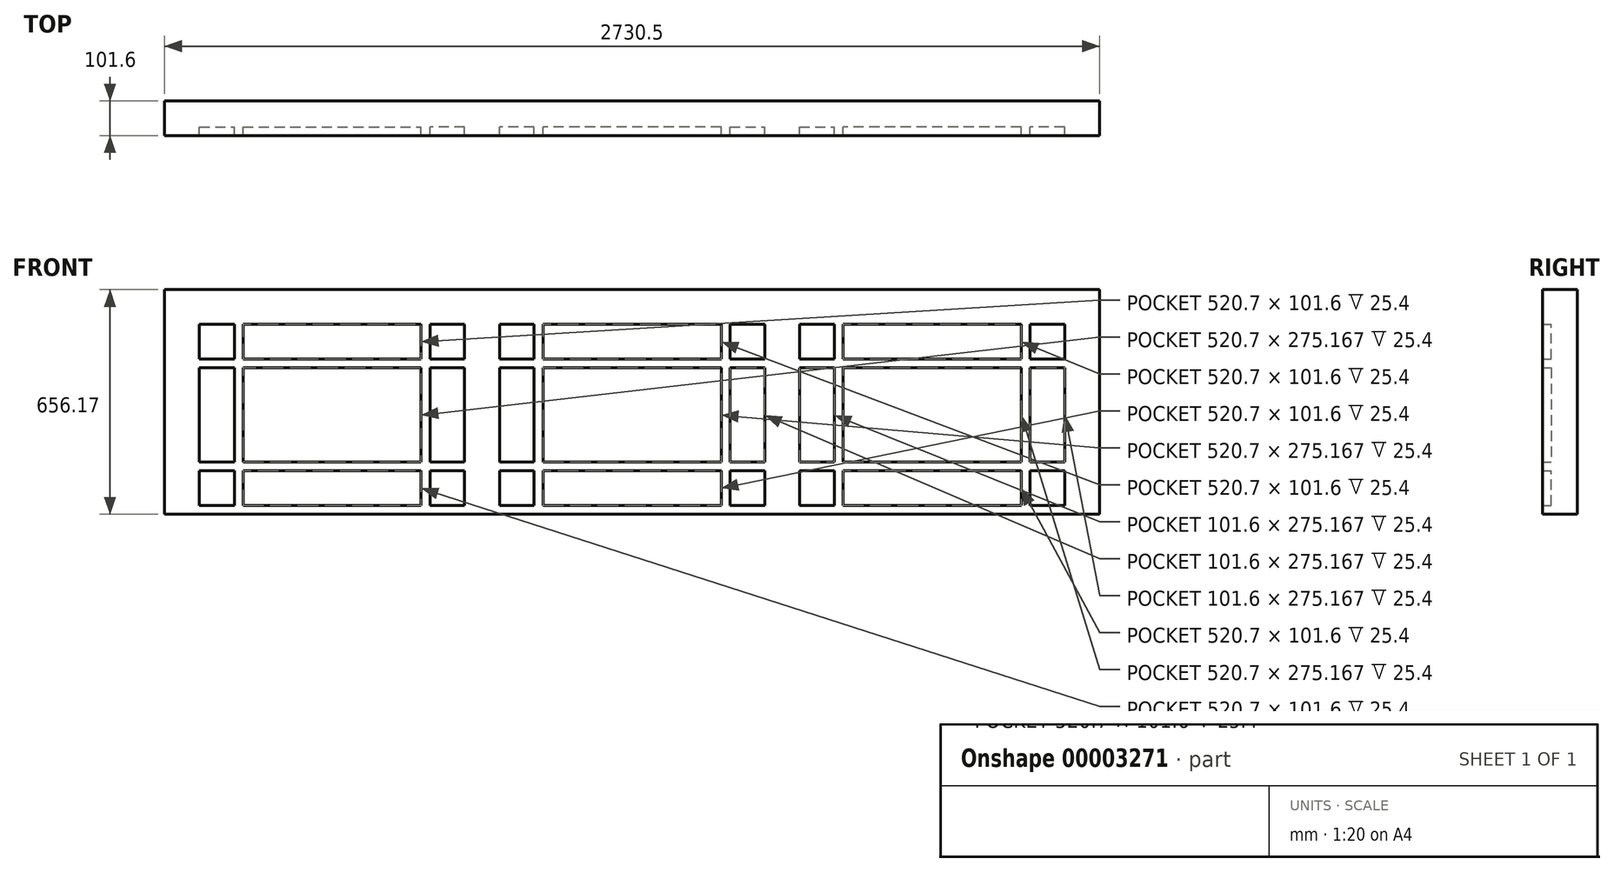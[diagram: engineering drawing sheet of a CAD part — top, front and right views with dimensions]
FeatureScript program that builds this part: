
annotation { "Feature Type Name" : "Feature", "Feature Type Description" : "" }
export const myFeature = defineFeature(function(context is Context, id is Id, definition is map)
    precondition{}
    {
        {
            var Q0;
            Q0=qCreatedBy(makeId("Front.planeOp"),FACE);
            var sketch = newSketch(context, id + "F0", { "sketchPlane" : qUnion([Q0])});
            skLineSegment(sketch, "E0.bottom", {"start": v(0, 0) * mm, "end": v(2730.5, 0) * mm});
            skLineSegment(sketch, "E0.top", {"start": v(0, 656.17) * mm, "end": v(2730.5, 656.17) * mm});
            skLineSegment(sketch, "E0.left", {"start": v(0, 0) * mm, "end": v(0, 656.17) * mm});
            skLineSegment(sketch, "E0.right", {"start": v(2730.5, 0) * mm, "end": v(2730.5, 656.17) * mm});
            skSolve(sketch);
        }
        {
            var Q0;
            Q0=makeQuery(id+"F0.imprint","IMPRINT",FACE,{"disambiguationData":[TD([[makeQuery(id+"F0.imprint","IMPRINT",EDGE,{"derivedFrom":sQuery(id+"F0.wireOp",EDGE,"E0.bottom")}),1.0]])]});
            extrude(context, id + "F1", {"entities" : qUnion([Q0]), "depth" : 76.2 * mm});
        }
        {
            var Q0;
            Q0=makeQuery(id+"F1.opExtrude","CAP_FACE",FACE,{"disambiguationData":[OSD([sQuery(id+"F0.wireOp",EDGE,"E0.bottom"),sQuery(id+"F0.wireOp",EDGE,"E0.top"),sQuery(id+"F0.wireOp",EDGE,"E0.left"),sQuery(id+"F0.wireOp",EDGE,"E0.right")])],"isStart":false});
            var sketch = newSketch(context, id + "F2", { "sketchPlane" : qUnion([Q0])});
            skLineSegment(sketch, "E1.0", {"start": v(2628.9, 25.4) * mm, "end": v(2628.9, 554.57) * mm, "construction": true});
            skLineSegment(sketch, "E1.1", {"start": v(101.6, 554.57) * mm, "end": v(876.3, 554.57) * mm, "construction": true});
            skLineSegment(sketch, "E1.2", {"start": v(101.6, 25.4) * mm, "end": v(101.6, 554.57) * mm, "construction": true});
            skLineSegment(sketch, "E2.0", {"start": v(101.6, 25.4) * mm, "end": v(876.3, 25.4) * mm, "construction": true});
            skLineSegment(sketch, "E3", {"start": v(876.3, 554.57) * mm, "end": v(876.3, 25.4) * mm, "construction": true});
            skLineSegment(sketch, "E4", {"start": v(977.9, 554.57) * mm, "end": v(977.9, 25.4) * mm, "construction": true});
            skLineSegment(sketch, "E5", {"start": v(1752.6, 554.57) * mm, "end": v(1752.6, 25.4) * mm, "construction": true});
            skLineSegment(sketch, "E6", {"start": v(1854.2, 554.57) * mm, "end": v(1854.2, 25.4) * mm, "construction": true});
            skLineSegment(sketch, "E7", {"start": v(876.3, 554.57) * mm, "end": v(977.9, 554.57) * mm, "construction": true});
            skLineSegment(sketch, "E8", {"start": v(977.9, 554.57) * mm, "end": v(1752.6, 554.57) * mm, "construction": true});
            skLineSegment(sketch, "E9", {"start": v(1752.6, 554.57) * mm, "end": v(1854.2, 554.57) * mm, "construction": true});
            skLineSegment(sketch, "E10", {"start": v(1854.2, 554.57) * mm, "end": v(2628.9, 554.57) * mm, "construction": true});
            skLineSegment(sketch, "E11", {"start": v(1854.2, 25.4) * mm, "end": v(2628.9, 25.4) * mm, "construction": true});
            skLineSegment(sketch, "E12", {"start": v(977.9, 25.4) * mm, "end": v(1752.6, 25.4) * mm, "construction": true});
            skLineSegment(sketch, "E13", {"start": v(101.6, 554.57) * mm, "end": v(0, 554.57) * mm, "construction": true});
            skPoint(sketch, "E14", {"position": v(488.95, 554.57) * mm});
            skLineSegment(sketch, "E15", {"start": v(488.95, 554.57) * mm, "end": v(488.95, 25.4) * mm, "construction": true});
            skPoint(sketch, "E16", {"position": v(927.1, 554.57) * mm});
            skLineSegment(sketch, "E17", {"start": v(927.1, 554.57) * mm, "end": v(927.1, 0) * mm, "construction": true});
            skPoint(sketch, "E18", {"position": v(101.6, 289.98) * mm});
            skLineSegment(sketch, "E19", {"start": v(101.6, 289.98) * mm, "end": v(876.3, 289.98) * mm, "construction": true});
            skLineSegment(sketch, "E20", {"start": v(101.6, 554.57) * mm, "end": v(203.2, 554.57) * mm});
            skLineSegment(sketch, "E21", {"start": v(203.2, 554.57) * mm, "end": v(203.2, 452.97) * mm});
            skLineSegment(sketch, "E22", {"start": v(203.2, 452.97) * mm, "end": v(101.6, 452.97) * mm});
            skLineSegment(sketch, "E23", {"start": v(101.6, 452.97) * mm, "end": v(101.6, 554.57) * mm});
            skLineSegment(sketch, "E24", {"start": v(488.95, 554.57) * mm, "end": v(228.6, 554.57) * mm});
            skLineSegment(sketch, "E25", {"start": v(228.6, 554.57) * mm, "end": v(228.6, 452.97) * mm});
            skLineSegment(sketch, "E26", {"start": v(228.6, 452.97) * mm, "end": v(488.95, 452.97) * mm});
            skLineSegment(sketch, "E27", {"start": v(203.2, 289.98) * mm, "end": v(203.2, 427.57) * mm});
            skLineSegment(sketch, "E28", {"start": v(203.2, 427.57) * mm, "end": v(101.6, 427.57) * mm});
            skLineSegment(sketch, "E29", {"start": v(101.6, 427.57) * mm, "end": v(101.6, 289.98) * mm});
            skLineSegment(sketch, "E30", {"start": v(203.2, 554.57) * mm, "end": v(228.6, 554.57) * mm, "construction": true});
            skLineSegment(sketch, "E31", {"start": v(101.6, 427.57) * mm, "end": v(101.6, 452.97) * mm, "construction": true});
            skLineSegment(sketch, "E32", {"start": v(203.2, 289.98) * mm, "end": v(228.6, 289.98) * mm, "construction": true});
            skLineSegment(sketch, "E33", {"start": v(228.6, 289.98) * mm, "end": v(228.6, 427.57) * mm});
            skLineSegment(sketch, "E34", {"start": v(228.6, 427.57) * mm, "end": v(488.95, 427.57) * mm});
            skLineSegment(sketch, "E35.0.MirrorCS", {"start": v(488.95, 25.4) * mm, "end": v(228.6, 25.4) * mm});
            skLineSegment(sketch, "E35.1.MirrorCS", {"start": v(228.6, 25.4) * mm, "end": v(228.6, 127) * mm});
            skLineSegment(sketch, "E35.2.MirrorCS", {"start": v(228.6, 127) * mm, "end": v(488.95, 127) * mm});
            skLineSegment(sketch, "E35.3.MirrorCS", {"start": v(228.6, 152.4) * mm, "end": v(488.95, 152.4) * mm});
            skLineSegment(sketch, "E35.4.MirrorCS", {"start": v(228.6, 289.98) * mm, "end": v(228.6, 152.4) * mm});
            skLineSegment(sketch, "E35.5.MirrorCS", {"start": v(203.2, 289.98) * mm, "end": v(203.2, 152.4) * mm});
            skLineSegment(sketch, "E35.6.MirrorCS", {"start": v(203.2, 152.4) * mm, "end": v(101.6, 152.4) * mm});
            skLineSegment(sketch, "E35.7.MirrorCS", {"start": v(101.6, 152.4) * mm, "end": v(101.6, 289.98) * mm});
            skLineSegment(sketch, "E35.8.MirrorCS", {"start": v(203.2, 127) * mm, "end": v(101.6, 127) * mm});
            skLineSegment(sketch, "E35.9.MirrorCS", {"start": v(203.2, 25.4) * mm, "end": v(203.2, 127) * mm});
            skLineSegment(sketch, "E35.10.MirrorCS", {"start": v(101.6, 127) * mm, "end": v(101.6, 25.4) * mm});
            skLineSegment(sketch, "E35.11.MirrorCS", {"start": v(101.6, 25.4) * mm, "end": v(203.2, 25.4) * mm});
            skLineSegment(sketch, "E36.0.MirrorCS", {"start": v(488.95, 554.57) * mm, "end": v(749.3, 554.57) * mm});
            skLineSegment(sketch, "E37.0.MirrorCS", {"start": v(749.3, 554.57) * mm, "end": v(749.3, 452.97) * mm});
            skLineSegment(sketch, "E38.0.MirrorCS", {"start": v(749.3, 452.97) * mm, "end": v(488.95, 452.97) * mm});
            skLineSegment(sketch, "E39.0.MirrorCS", {"start": v(749.3, 427.57) * mm, "end": v(488.95, 427.57) * mm});
            skLineSegment(sketch, "E40.0.MirrorCS", {"start": v(749.3, 289.98) * mm, "end": v(749.3, 427.57) * mm});
            skLineSegment(sketch, "E41.0.MirrorCS", {"start": v(749.3, 289.98) * mm, "end": v(749.3, 152.4) * mm});
            skLineSegment(sketch, "E42.0.MirrorCS", {"start": v(749.3, 152.4) * mm, "end": v(488.95, 152.4) * mm});
            skLineSegment(sketch, "E43.0.MirrorCS", {"start": v(749.3, 127) * mm, "end": v(488.95, 127) * mm});
            skLineSegment(sketch, "E44.0.MirrorCS", {"start": v(749.3, 25.4) * mm, "end": v(749.3, 127) * mm});
            skLineSegment(sketch, "E45.0.MirrorCS", {"start": v(488.95, 25.4) * mm, "end": v(749.3, 25.4) * mm});
            skLineSegment(sketch, "E46.0.MirrorCS", {"start": v(876.3, 25.4) * mm, "end": v(774.7, 25.4) * mm});
            skLineSegment(sketch, "E47.0.MirrorCS", {"start": v(876.3, 127) * mm, "end": v(876.3, 25.4) * mm});
            skLineSegment(sketch, "E48.0.MirrorCS", {"start": v(774.7, 127) * mm, "end": v(876.3, 127) * mm});
            skLineSegment(sketch, "E49.0.MirrorCS", {"start": v(774.7, 25.4) * mm, "end": v(774.7, 127) * mm});
            skLineSegment(sketch, "E50.0.MirrorCS", {"start": v(774.7, 152.4) * mm, "end": v(876.3, 152.4) * mm});
            skLineSegment(sketch, "E51.0.MirrorCS", {"start": v(876.3, 152.4) * mm, "end": v(876.3, 289.98) * mm});
            skLineSegment(sketch, "E52.0.MirrorCS", {"start": v(876.3, 427.57) * mm, "end": v(876.3, 289.98) * mm});
            skLineSegment(sketch, "E53.0.MirrorCS", {"start": v(774.7, 427.57) * mm, "end": v(876.3, 427.57) * mm});
            skLineSegment(sketch, "E54.0.MirrorCS", {"start": v(774.7, 452.97) * mm, "end": v(876.3, 452.97) * mm});
            skLineSegment(sketch, "E55.0.MirrorCS", {"start": v(876.3, 452.97) * mm, "end": v(876.3, 554.57) * mm});
            skLineSegment(sketch, "E56.0.MirrorCS", {"start": v(876.3, 554.57) * mm, "end": v(774.7, 554.57) * mm});
            skLineSegment(sketch, "E57.0.MirrorCS", {"start": v(774.7, 554.57) * mm, "end": v(774.7, 452.97) * mm});
            skLineSegment(sketch, "E58.0.MirrorCS", {"start": v(774.7, 289.98) * mm, "end": v(774.7, 427.57) * mm});
            skLineSegment(sketch, "E59.0.MirrorCS", {"start": v(774.7, 289.98) * mm, "end": v(774.7, 152.4) * mm});
            skPoint(sketch, "E60", {"position": v(1365.25, 656.17) * mm});
            skLineSegment(sketch, "E61", {"start": v(1365.25, 656.17) * mm, "end": v(1365.25, 0) * mm, "construction": true});
            skLineSegment(sketch, "E62.0.MirrorCS", {"start": v(1854.2, 25.4) * mm, "end": v(1955.8, 25.4) * mm});
            skLineSegment(sketch, "E63.0.MirrorCS", {"start": v(2241.55, 25.4) * mm, "end": v(1981.2, 25.4) * mm});
            skLineSegment(sketch, "E64.0.MirrorCS", {"start": v(2241.55, 25.4) * mm, "end": v(2501.9, 25.4) * mm});
            skLineSegment(sketch, "E65.0.MirrorCS", {"start": v(2628.9, 25.4) * mm, "end": v(2527.3, 25.4) * mm});
            skLineSegment(sketch, "E66.0.MirrorCS", {"start": v(1854.2, 554.57) * mm, "end": v(1955.8, 554.57) * mm});
            skLineSegment(sketch, "E67.0.MirrorCS", {"start": v(2241.55, 554.57) * mm, "end": v(1981.2, 554.57) * mm});
            skLineSegment(sketch, "E68.0.MirrorCS", {"start": v(2241.55, 554.57) * mm, "end": v(2501.9, 554.57) * mm});
            skLineSegment(sketch, "E69.0.MirrorCS", {"start": v(2501.9, 452.97) * mm, "end": v(2241.55, 452.97) * mm});
            skLineSegment(sketch, "E70.0.MirrorCS", {"start": v(1981.2, 127) * mm, "end": v(2241.55, 127) * mm});
            skLineSegment(sketch, "E71.0.MirrorCS", {"start": v(1955.8, 289.98) * mm, "end": v(1955.8, 152.4) * mm});
            skLineSegment(sketch, "E72.0.MirrorCS", {"start": v(1854.2, 152.4) * mm, "end": v(1854.2, 289.98) * mm});
            skLineSegment(sketch, "E73.0.MirrorCS", {"start": v(1955.8, 152.4) * mm, "end": v(1854.2, 152.4) * mm});
            skLineSegment(sketch, "E74.0.MirrorCS", {"start": v(1955.8, 289.98) * mm, "end": v(1955.8, 427.57) * mm});
            skLineSegment(sketch, "E75.0.MirrorCS", {"start": v(1854.2, 427.57) * mm, "end": v(1854.2, 289.98) * mm});
            skLineSegment(sketch, "E76.0.MirrorCS", {"start": v(1854.2, 452.97) * mm, "end": v(1854.2, 554.57) * mm});
            skLineSegment(sketch, "E77.0.MirrorCS", {"start": v(1955.8, 554.57) * mm, "end": v(1955.8, 452.97) * mm});
            skLineSegment(sketch, "E78.0.MirrorCS", {"start": v(1981.2, 554.57) * mm, "end": v(1981.2, 452.97) * mm});
            skLineSegment(sketch, "E79.0.MirrorCS", {"start": v(1981.2, 452.97) * mm, "end": v(2241.55, 452.97) * mm});
            skLineSegment(sketch, "E80.0.MirrorCS", {"start": v(2501.9, 554.57) * mm, "end": v(2501.9, 452.97) * mm});
            skLineSegment(sketch, "E81.0.MirrorCS", {"start": v(2527.3, 554.57) * mm, "end": v(2527.3, 452.97) * mm});
            skLineSegment(sketch, "E82.0.MirrorCS", {"start": v(2628.9, 554.57) * mm, "end": v(2527.3, 554.57) * mm});
            skLineSegment(sketch, "E83.0.MirrorCS", {"start": v(2628.9, 452.97) * mm, "end": v(2628.9, 554.57) * mm});
            skLineSegment(sketch, "E84.0.MirrorCS", {"start": v(2527.3, 452.97) * mm, "end": v(2628.9, 452.97) * mm});
            skLineSegment(sketch, "E85.0.MirrorCS", {"start": v(2527.3, 427.57) * mm, "end": v(2628.9, 427.57) * mm});
            skLineSegment(sketch, "E86.0.MirrorCS", {"start": v(2628.9, 427.57) * mm, "end": v(2628.9, 289.98) * mm});
            skLineSegment(sketch, "E87.0.MirrorCS", {"start": v(1955.8, 127) * mm, "end": v(1854.2, 127) * mm});
            skLineSegment(sketch, "E88.0.MirrorCS", {"start": v(1955.8, 25.4) * mm, "end": v(1955.8, 127) * mm});
            skLineSegment(sketch, "E89.0.MirrorCS", {"start": v(1981.2, 25.4) * mm, "end": v(1981.2, 127) * mm});
            skLineSegment(sketch, "E90.0.MirrorCS", {"start": v(2628.9, 152.4) * mm, "end": v(2628.9, 289.98) * mm});
            skLineSegment(sketch, "E91.0.MirrorCS", {"start": v(2527.3, 152.4) * mm, "end": v(2628.9, 152.4) * mm});
            skLineSegment(sketch, "E92.0.MirrorCS", {"start": v(2501.9, 152.4) * mm, "end": v(2241.55, 152.4) * mm});
            skLineSegment(sketch, "E93.0.MirrorCS", {"start": v(1981.2, 152.4) * mm, "end": v(2241.55, 152.4) * mm});
            skLineSegment(sketch, "E94.0.MirrorCS", {"start": v(1981.2, 289.98) * mm, "end": v(1981.2, 152.4) * mm});
            skLineSegment(sketch, "E95.0.MirrorCS", {"start": v(1981.2, 289.98) * mm, "end": v(1981.2, 427.57) * mm});
            skLineSegment(sketch, "E96.0.MirrorCS", {"start": v(1981.2, 427.57) * mm, "end": v(2241.55, 427.57) * mm});
            skLineSegment(sketch, "E97.0.MirrorCS", {"start": v(2501.9, 427.57) * mm, "end": v(2241.55, 427.57) * mm});
            skLineSegment(sketch, "E98.0.MirrorCS", {"start": v(2501.9, 289.98) * mm, "end": v(2501.9, 427.57) * mm});
            skLineSegment(sketch, "E99.0.MirrorCS", {"start": v(2501.9, 289.98) * mm, "end": v(2501.9, 152.4) * mm});
            skLineSegment(sketch, "E100.0.MirrorCS", {"start": v(2501.9, 127) * mm, "end": v(2241.55, 127) * mm});
            skLineSegment(sketch, "E101.0.MirrorCS", {"start": v(2501.9, 25.4) * mm, "end": v(2501.9, 127) * mm});
            skLineSegment(sketch, "E102.0.MirrorCS", {"start": v(2527.3, 25.4) * mm, "end": v(2527.3, 127) * mm});
            skLineSegment(sketch, "E103.0.MirrorCS", {"start": v(2628.9, 127) * mm, "end": v(2628.9, 25.4) * mm});
            skLineSegment(sketch, "E104.0.MirrorCS", {"start": v(2527.3, 127) * mm, "end": v(2628.9, 127) * mm});
            skLineSegment(sketch, "E105.0.MirrorCS", {"start": v(2527.3, 289.98) * mm, "end": v(2527.3, 152.4) * mm});
            skLineSegment(sketch, "E106.0.MirrorCS", {"start": v(2527.3, 289.98) * mm, "end": v(2527.3, 427.57) * mm});
            skLineSegment(sketch, "E107", {"start": v(1854.2, 127) * mm, "end": v(1854.2, 25.4) * mm});
            skPoint(sketch, "E108", {"position": v(1803.4, 554.57) * mm});
            skLineSegment(sketch, "E109", {"start": v(1803.4, 554.57) * mm, "end": v(1803.4, 0) * mm, "construction": true});
            skLineSegment(sketch, "E110.0.MirrorCS", {"start": v(1625.6, 427.57) * mm, "end": v(1365.25, 427.57) * mm});
            skLineSegment(sketch, "E111.0.MirrorCS", {"start": v(1625.6, 289.98) * mm, "end": v(1625.6, 427.57) * mm});
            skLineSegment(sketch, "E112.0.MirrorCS", {"start": v(1625.6, 289.98) * mm, "end": v(1625.6, 152.4) * mm});
            skLineSegment(sketch, "E113.0.MirrorCS", {"start": v(1625.6, 152.4) * mm, "end": v(1365.25, 152.4) * mm});
            skLineSegment(sketch, "E114.0.MirrorCS", {"start": v(1104.9, 152.4) * mm, "end": v(1365.25, 152.4) * mm});
            skLineSegment(sketch, "E115.0.MirrorCS", {"start": v(977.9, 127) * mm, "end": v(977.9, 25.4) * mm});
            skLineSegment(sketch, "E116.0.MirrorCS", {"start": v(977.9, 152.4) * mm, "end": v(977.9, 289.98) * mm});
            skLineSegment(sketch, "E117.0.MirrorCS", {"start": v(977.9, 427.57) * mm, "end": v(977.9, 289.98) * mm});
            skLineSegment(sketch, "E118.0.MirrorCS", {"start": v(977.9, 452.97) * mm, "end": v(977.9, 554.57) * mm});
            skLineSegment(sketch, "E119.0.MirrorCS", {"start": v(977.9, 554.57) * mm, "end": v(1079.5, 554.57) * mm});
            skLineSegment(sketch, "E120.0.MirrorCS", {"start": v(1079.5, 554.57) * mm, "end": v(1079.5, 452.97) * mm});
            skLineSegment(sketch, "E121.0.MirrorCS", {"start": v(1625.6, 127) * mm, "end": v(1365.25, 127) * mm});
            skLineSegment(sketch, "E122.0.MirrorCS", {"start": v(1104.9, 127) * mm, "end": v(1365.25, 127) * mm});
            skLineSegment(sketch, "E123.0.MirrorCS", {"start": v(1104.9, 25.4) * mm, "end": v(1104.9, 127) * mm});
            skLineSegment(sketch, "E124.0.MirrorCS", {"start": v(1365.25, 25.4) * mm, "end": v(1104.9, 25.4) * mm});
            skLineSegment(sketch, "E125.0.MirrorCS", {"start": v(1365.25, 25.4) * mm, "end": v(1625.6, 25.4) * mm});
            skLineSegment(sketch, "E126.0.MirrorCS", {"start": v(1079.5, 289.98) * mm, "end": v(1079.5, 152.4) * mm});
            skLineSegment(sketch, "E127.0.MirrorCS", {"start": v(1079.5, 289.98) * mm, "end": v(1079.5, 427.57) * mm});
            skLineSegment(sketch, "E128.0.MirrorCS", {"start": v(1079.5, 427.57) * mm, "end": v(977.9, 427.57) * mm});
            skLineSegment(sketch, "E129.0.MirrorCS", {"start": v(1079.5, 152.4) * mm, "end": v(977.9, 152.4) * mm});
            skLineSegment(sketch, "E130.0.MirrorCS", {"start": v(1104.9, 554.57) * mm, "end": v(1104.9, 452.97) * mm});
            skLineSegment(sketch, "E131.0.MirrorCS", {"start": v(1365.25, 554.57) * mm, "end": v(1104.9, 554.57) * mm});
            skLineSegment(sketch, "E132.0.MirrorCS", {"start": v(1752.6, 554.57) * mm, "end": v(1651, 554.57) * mm});
            skLineSegment(sketch, "E133.0.MirrorCS", {"start": v(1752.6, 152.4) * mm, "end": v(1752.6, 289.98) * mm});
            skLineSegment(sketch, "E134.0.MirrorCS", {"start": v(1752.6, 427.57) * mm, "end": v(1752.6, 289.98) * mm});
            skLineSegment(sketch, "E135.0.MirrorCS", {"start": v(1651, 554.57) * mm, "end": v(1651, 452.97) * mm});
            skLineSegment(sketch, "E136.0.MirrorCS", {"start": v(1079.5, 127) * mm, "end": v(977.9, 127) * mm});
            skLineSegment(sketch, "E137.0.MirrorCS", {"start": v(1079.5, 25.4) * mm, "end": v(1079.5, 127) * mm});
            skLineSegment(sketch, "E138.0.MirrorCS", {"start": v(977.9, 25.4) * mm, "end": v(1079.5, 25.4) * mm});
            skLineSegment(sketch, "E139.0.MirrorCS", {"start": v(1104.9, 427.57) * mm, "end": v(1365.25, 427.57) * mm});
            skLineSegment(sketch, "E140.0.MirrorCS", {"start": v(1625.6, 554.57) * mm, "end": v(1625.6, 452.97) * mm});
            skLineSegment(sketch, "E141.0.MirrorCS", {"start": v(1365.25, 554.57) * mm, "end": v(1625.6, 554.57) * mm});
            skLineSegment(sketch, "E142.0.MirrorCS", {"start": v(1651, 289.98) * mm, "end": v(1651, 427.57) * mm});
            skLineSegment(sketch, "E143.0.MirrorCS", {"start": v(1651, 289.98) * mm, "end": v(1651, 152.4) * mm});
            skLineSegment(sketch, "E144.0.MirrorCS", {"start": v(1651, 427.57) * mm, "end": v(1752.6, 427.57) * mm});
            skLineSegment(sketch, "E145.0.MirrorCS", {"start": v(1625.6, 25.4) * mm, "end": v(1625.6, 127) * mm});
            skLineSegment(sketch, "E146.0.MirrorCS", {"start": v(1651, 25.4) * mm, "end": v(1651, 127) * mm});
            skLineSegment(sketch, "E147.0.MirrorCS", {"start": v(1752.6, 127) * mm, "end": v(1752.6, 25.4) * mm});
            skLineSegment(sketch, "E148.0.MirrorCS", {"start": v(1651, 127) * mm, "end": v(1752.6, 127) * mm});
            skLineSegment(sketch, "E149.0.MirrorCS", {"start": v(1752.6, 25.4) * mm, "end": v(1651, 25.4) * mm});
            skLineSegment(sketch, "E150.0.MirrorCS", {"start": v(1651, 152.4) * mm, "end": v(1752.6, 152.4) * mm});
            skLineSegment(sketch, "E151.0.MirrorCS", {"start": v(1079.5, 452.97) * mm, "end": v(977.9, 452.97) * mm});
            skLineSegment(sketch, "E152.0.MirrorCS", {"start": v(1104.9, 289.98) * mm, "end": v(1104.9, 427.57) * mm});
            skLineSegment(sketch, "E153.0.MirrorCS", {"start": v(1104.9, 289.98) * mm, "end": v(1104.9, 152.4) * mm});
            skLineSegment(sketch, "E154.0.MirrorCS", {"start": v(1104.9, 452.97) * mm, "end": v(1365.25, 452.97) * mm});
            skLineSegment(sketch, "E155.0.MirrorCS", {"start": v(1625.6, 452.97) * mm, "end": v(1365.25, 452.97) * mm});
            skLineSegment(sketch, "E156.0.MirrorCS", {"start": v(1651, 452.97) * mm, "end": v(1752.6, 452.97) * mm});
            skLineSegment(sketch, "E157.0.MirrorCS", {"start": v(1752.6, 452.97) * mm, "end": v(1752.6, 554.57) * mm});
            skLineSegment(sketch, "E158.0.MirrorCS", {"start": v(1955.8, 452.97) * mm, "end": v(1854.2, 452.97) * mm});
            skLineSegment(sketch, "E159.0.MirrorCS", {"start": v(1955.8, 427.57) * mm, "end": v(1854.2, 427.57) * mm});
            skLineSegment(sketch, "E160.0", {"start": v(0, 0) * mm, "end": v(0, 656.17) * mm});
            skLineSegment(sketch, "E160.1", {"start": v(0, 656.17) * mm, "end": v(2730.5, 656.17) * mm});
            skLineSegment(sketch, "E160.2", {"start": v(2730.5, 0) * mm, "end": v(2730.5, 656.17) * mm});
            skLineSegment(sketch, "E160.3", {"start": v(0, 0) * mm, "end": v(2730.5, 0) * mm});
            skSolve(sketch);
        }
        {
            var Q0;
            Q0=makeQuery(id+"F2.imprint","IMPRINT",FACE,{"disambiguationData":[TD([[makeQuery(id+"F2.imprint","IMPRINT",EDGE,{"derivedFrom":sQuery(id+"F2.wireOp",EDGE,"E20")}),1.0]])]});
            extrude(context, id + "F3", {"entities" : qUnion([Q0]), "operationType" : NewBodyOperationType.ADD, "depth" : 25.4 * mm});
        }
    });
